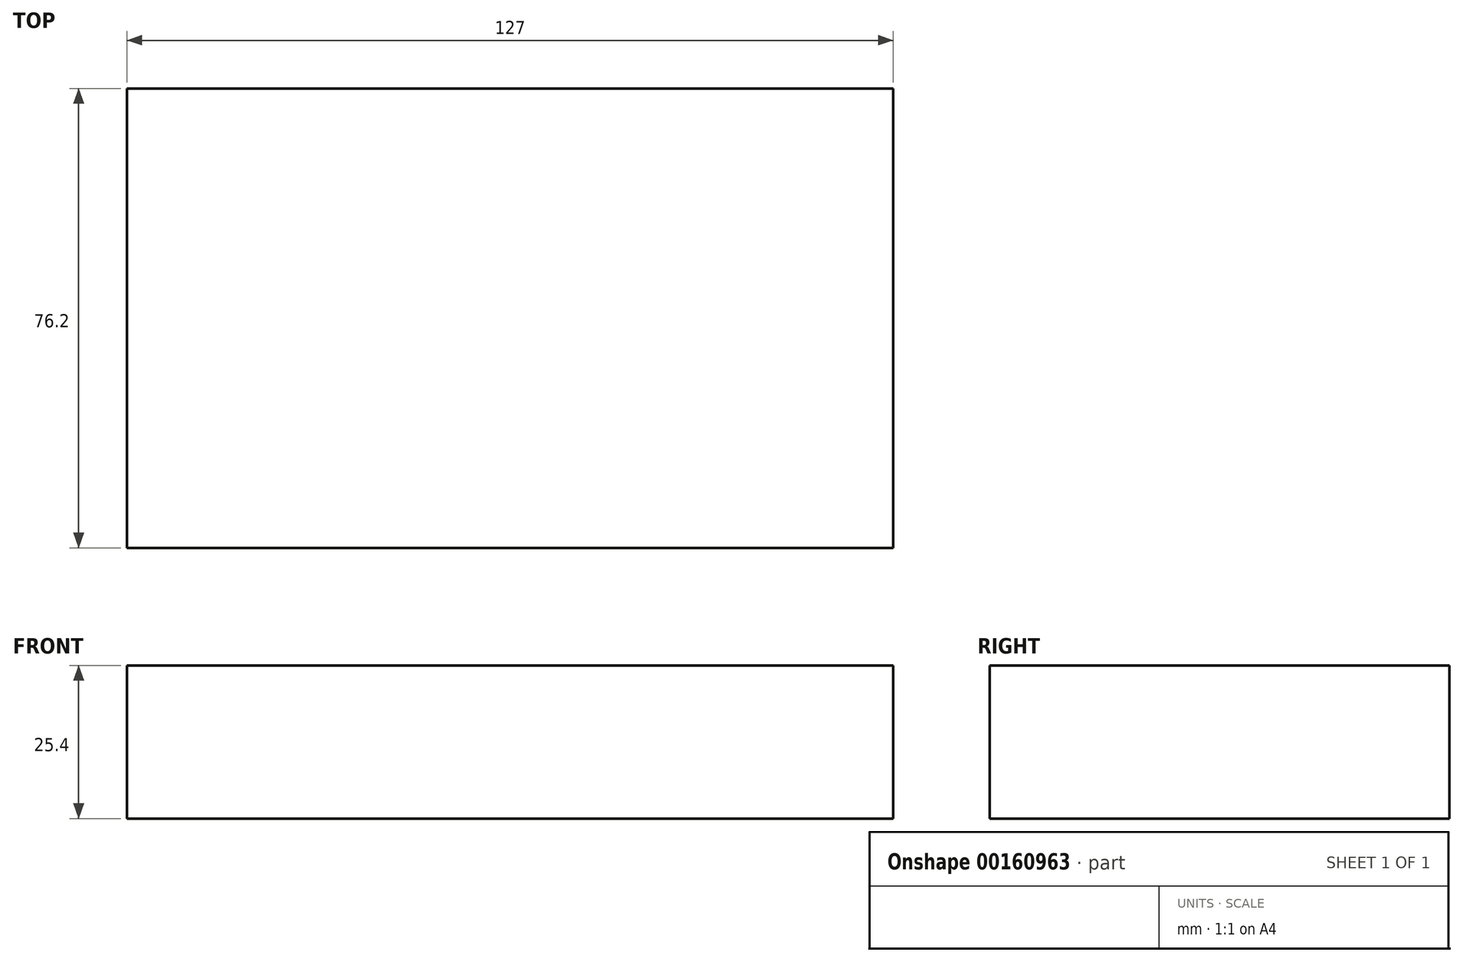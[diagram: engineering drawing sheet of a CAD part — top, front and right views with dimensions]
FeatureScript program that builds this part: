
annotation { "Feature Type Name" : "Feature", "Feature Type Description" : "" }
export const myFeature = defineFeature(function(context is Context, id is Id, definition is map)
    precondition{}
    {
        {
            var Q0;
            Q0=qCreatedBy(makeId("Top.planeOp"),FACE);
            var sketch = newSketch(context, id + "F0", { "sketchPlane" : qUnion([Q0])});
            skLineSegment(sketch, "E0.bottom", {"start": v(63.5, 38.1) * mm, "end": v(-63.5, 38.1) * mm});
            skLineSegment(sketch, "E0.top", {"start": v(63.5, -38.1) * mm, "end": v(-63.5, -38.1) * mm});
            skLineSegment(sketch, "E0.left", {"start": v(63.5, 38.1) * mm, "end": v(63.5, -38.1) * mm});
            skLineSegment(sketch, "E0.right", {"start": v(-63.5, 38.1) * mm, "end": v(-63.5, -38.1) * mm});
            skPoint(sketch, "E0.middle", {"position": v(0, 0) * mm});
            skSolve(sketch);
        }
        {
            var Q0;
            Q0=makeQuery(id+"F0.imprint","IMPRINT",FACE,{"disambiguationData":[TD([[makeQuery(id+"F0.imprint","IMPRINT",EDGE,{"derivedFrom":sQuery(id+"F0.wireOp",EDGE,"E0.bottom")}),1.0]])]});
            extrude(context, id + "F1", {"entities" : qUnion([Q0]), "depth" : 25.4 * mm});
        }
    });
